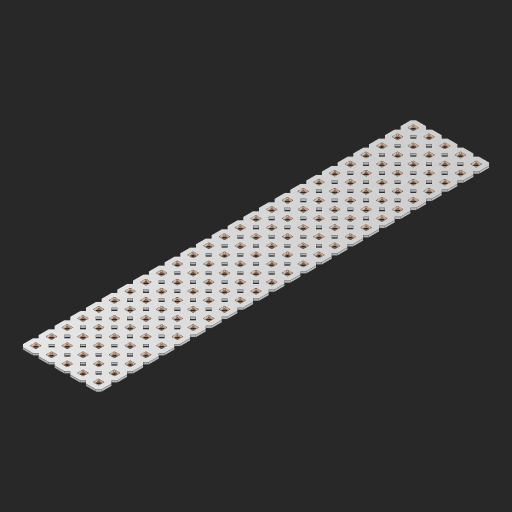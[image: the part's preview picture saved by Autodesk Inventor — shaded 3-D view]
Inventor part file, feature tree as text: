
AUTODESK INVENTOR PART (.ipt)
format: ipt  version: 2023 (Build 270158000, 158)  size: 1,711,616 bytes
history: native  units: in
note: dims shown in document units (in); Inventor stores cm internally (conversion verified against a paired STEP export)
features: other x357, extrude x124, sketch x2, pattern_linear x1
ambient origin geometry x8: Origin, YZ Plane, XZ Plane, XY Plane, X Axis, Y Axis, Z Axis, Center Point
bodies: Solid1 (feature_tree), Body (feature_tree)
feature tree (484):
  other  "Table"
  other  "Alu Plate 5x25"
  other  "Alu Plate 5x24"
  other  "Alu Plate 5x23"
  other  "Alu Plate 5x22"
  other  "Alu Plate 5x21"
  other  "Alu Plate 5x20"
  other  "Alu Plate 5x19"
  other  "Alu Plate 5x18"
  other  "Alu Plate 5x17"
  other  "Alu Plate 5x16"
  other  "Alu Plate 5x15"
  other  "Alu Plate 5x14"
  other  "Alu Plate 5x13"
  other  "Alu Plate 5x12"
  other  "Alu Plate 5x11"
  other  "Alu Plate 5x10"
  other  "Alu Plate 5x9"
  other  "Alu Plate 5x8"
  other  "Alu Plate 5x7"
  other  "Alu Plate 5x6"
  other  "Alu Plate 5x5"
  other  "Alu Plate 4x25"
  other  "Alu Plate 4x24"
  other  "Alu Plate 4x23"
  other  "Alu Plate 4x22"
  other  "Alu Plate 4x21"
  other  "Alu Plate 4x20"
  other  "Alu Plate 4x19"
  other  "Alu Plate 4x18"
  other  "Alu Plate 4x17"
  other  "Alu Plate 4x16"
  other  "Alu Plate 4x15"
  other  "Alu Plate 4x14"
  other  "Alu Plate 4x13"
  other  "Alu Plate 4x12"
  other  "Alu Plate 4x11"
  other  "Alu Plate 4x10"
  other  "Alu Plate 4x9"
  other  "Alu Plate 4x8"
  other  "Alu Plate 4x7"
  other  "Alu Plate 4x6"
  other  "Alu Plate 4x5"
  other  "Alu Plate 4x4"
  other  "Alu Plate 3x25"
  other  "Alu Plate 3x24"
  other  "Alu Plate 3x23"
  other  "Alu Plate 3x22"
  other  "Alu Plate 3x21"
  other  "Alu Plate 3x20"
  other  "Alu Plate 3x19"
  other  "Alu Plate 3x18"
  other  "Alu Plate 3x17"
  other  "Alu Plate 3x16"
  other  "Alu Plate 3x15"
  other  "Alu Plate 3x14"
  other  "Alu Plate 3x13"
  other  "Alu Plate 3x12"
  other  "Alu Plate 3x11"
  other  "Alu Plate 3x10"
  other  "Alu Plate 3x9"
  other  "Alu Plate 3x8"
  other  "Alu Plate 3x7"
  other  "Alu Plate 3x6"
  other  "Alu Plate 3x5"
  other  "Alu Plate 3x4"
  other  "Alu Plate 3x3"
  other  "Alu Plate 2x25"
  other  "Alu Plate 2x24"
  other  "Alu Plate 2x23"
  other  "Alu Plate 2x22"
  other  "Alu Plate 2x21"
  other  "Alu Plate 2x20"
  other  "Alu Plate 2x19"
  other  "Alu Plate 2x18"
  other  "Alu Plate 2x17"
  other  "Alu Plate 2x16"
  other  "Alu Plate 2x15"
  other  "Alu Plate 2x14"
  other  "Alu Plate 2x13"
  other  "Alu Plate 2x12"
  other  "Alu Plate 2x11"
  other  "Alu Plate 2x10"
  other  "Alu Plate 2x9"
  other  "Alu Plate 2x8"
  other  "Alu Plate 2x7"
  other  "Alu Plate 2x6"
  other  "Alu Plate 2x5"
  other  "Alu Plate 2x4"
  other  "Alu Plate 2x3"
  other  "Alu Plate 2x2"
  other  "Alu Plate 1x25"
  other  "Alu Plate 1x24"
  other  "Alu Plate 1x23"
  other  "Alu Plate 1x22"
  other  "Alu Plate 1x21"
  other  "Alu Plate 1x20"
  other  "Alu Plate 1x19"
  other  "Alu Plate 1x18"
  other  "Alu Plate 1x17"
  other  "Alu Plate 1x16"
  other  "Alu Plate 1x15"
  other  "Alu Plate 1x14"
  other  "Alu Plate 1x13"
  other  "Alu Plate 1x12"
  other  "Alu Plate 1x11"
  other  "Alu Plate 1x10"
  other  "Alu Plate 1x9"
  other  "Alu Plate 1x8"
  other  "Alu Plate 1x7"
  other  "Alu Plate 1x6"
  other  "Alu Plate 1x5"
  other  "Alu Plate 1x4"
  other  "Alu Plate 1x3"
  other  "Alu Plate 1x2"
  other  "Alu Plate 1x1"
  other  "Steel Plate 5x25"
  other  "Steel Plate 5x24"
  other  "Steel Plate 5x23"
  other  "Steel Plate 5x22"
  other  "Steel Plate 5x21"
  other  "Steel Plate 5x20"
  other  "Steel Plate 5x19"
  other  "Steel Plate 5x18"
  other  "Steel Plate 5x17"
  other  "Steel Plate 5x16"
  other  "Steel Plate 5x15"
  other  "Steel Plate 5x14"
  other  "Steel Plate 5x13"
  other  "Steel Plate 5x12"
  other  "Steel Plate 5x11"
  other  "Steel Plate 5x10"
  other  "Steel Plate 5x9"
  other  "Steel Plate 5x8"
  other  "Steel Plate 5x7"
  other  "Steel Plate 5x6"
  other  "Steel Plate 5x5"
  other  "Steel Plate 4x25"
  other  "Steel Plate 4x24"
  other  "Steel Plate 4x23"
  other  "Steel Plate 4x22"
  other  "Steel Plate 4x21"
  other  "Steel Plate 4x20"
  other  "Steel Plate 4x19"
  other  "Steel Plate 4x18"
  other  "Steel Plate 4x17"
  other  "Steel Plate 4x16"
  other  "Steel Plate 4x15"
  other  "Steel Plate 4x14"
  other  "Steel Plate 4x13"
  other  "Steel Plate 4x12"
  other  "Steel Plate 4x11"
  other  "Steel Plate 4x10"
  other  "Steel Plate 4x9"
  other  "Steel Plate 4x8"
  other  "Steel Plate 4x7"
  other  "Steel Plate 4x6"
  other  "Steel Plate 4x5"
  other  "Steel Plate 4x4"
  other  "Steel Plate 3x25"
  other  "Steel Plate 3x24"
  other  "Steel Plate 3x23"
  other  "Steel Plate 3x22"
  other  "Steel Plate 3x21"
  other  "Steel Plate 3x20"
  other  "Steel Plate 3x19"
  other  "Steel Plate 3x18"
  other  "Steel Plate 3x17"
  other  "Steel Plate 3x16"
  other  "Steel Plate 3x15"
  other  "Steel Plate 3x14"
  other  "Steel Plate 3x13"
  other  "Steel Plate 3x12"
  other  "Steel Plate 3x11"
  other  "Steel Plate 3x10"
  other  "Steel Plate 3x9"
  other  "Steel Plate 3x8"
  other  "Steel Plate 3x7"
  other  "Steel Plate 3x6"
  other  "Steel Plate 3x5"
  other  "Steel Plate 3x4"
  other  "Steel Plate 3x3"
  other  "Steel Plate 2x25"
  other  "Steel Plate 2x24"
  other  "Steel Plate 2x23"
  other  "Steel Plate 2x22"
  other  "Steel Plate 2x21"
  other  "Steel Plate 2x20"
  other  "Steel Plate 2x19"
  other  "Steel Plate 2x18"
  other  "Steel Plate 2x17"
  other  "Steel Plate 2x16"
  other  "Steel Plate 2x15"
  other  "Steel Plate 2x14"
  other  "Steel Plate 2x13"
  other  "Steel Plate 2x12"
  other  "Steel Plate 2x11"
  other  "Steel Plate 2x10"
  other  "Steel Plate 2x9"
  other  "Steel Plate 2x8"
  other  "Steel Plate 2x7"
  other  "Steel Plate 2x6"
  other  "Steel Plate 2x5"
  other  "Steel Plate 2x4"
  other  "Steel Plate 2x3"
  other  "Steel Plate 2x2"
  other  "Steel Plate 1x25"
  other  "Steel Plate 1x24"
  other  "Steel Plate 1x23"
  other  "Steel Plate 1x22"
  other  "Steel Plate 1x21"
  other  "Steel Plate 1x20"
  other  "Steel Plate 1x19"
  other  "Steel Plate 1x18"
  other  "Steel Plate 1x17"
  other  "Steel Plate 1x16"
  other  "Steel Plate 1x15"
  other  "Steel Plate 1x14"
  other  "Steel Plate 1x13"
  other  "Steel Plate 1x12"
  other  "Steel Plate 1x11"
  other  "Steel Plate 1x10"
  other  "Steel Plate 1x9"
  other  "Steel Plate 1x8"
  other  "Steel Plate 1x7"
  other  "Steel Plate 1x6"
  other  "Steel Plate 1x5"
  other  "Steel Plate 1x4"
  other  "Steel Plate 1x3"
  other  "Steel Plate 1x2"
  other  "Steel Plate 1x1"
  pattern_linear  "Rectangular Pattern1"  Spacing1=0.09in  [1 undecoded]
  sketch  "Sketch1"  dims[d1=0.5in]
  sketch  "Sketch2"  dims[d2=0.182in d3=0.09in d4=0.09in d5=0.09in d6=0.09in d7=0.09in d8=0.09in d9=0.09in d10=0.09in d11=0.02in d13=0.0in d14=0.172in d15=0.0625in d16=0.0in d19=0.5in d22=0.5in]
  other  "Srf1"
  other  "Srf126"
  other  "Srf127"
  other  "Srf128"
  other  "Srf129"
  other  "Srf130"
  other  "Srf131"
  other  "Srf250"
  other  "Srf251"
  other  "Srf252"
  other  "Srf253"
  other  "Srf254"
  other  "Srf255"
  other  "Srf256"
  other  "Srf257"
  other  "Srf258"
  other  "Srf259"
  other  "Srf260"
  other  "Srf261"
  other  "Srf262"
  other  "Srf263"
  other  "Srf264"
  other  "Srf265"
  other  "Srf266"
  other  "Srf267"
  other  "Srf268"
  other  "Srf269"
  other  "Srf270"
  other  "Srf271"
  other  "Srf272"
  other  "Srf273"
  other  "Srf274"
  other  "Srf275"
  other  "Srf276"
  other  "Srf277"
  other  "Srf278"
  other  "Srf279"
  other  "Srf280"
  other  "Srf281"
  other  "Srf282"
  other  "Srf283"
  other  "Srf284"
  other  "Srf285"
  other  "Srf286"
  other  "Srf287"
  other  "Srf288"
  other  "Srf289"
  other  "Srf290"
  other  "Srf291"
  other  "Srf292"
  other  "Srf293"
  other  "Srf294"
  other  "Srf295"
  other  "Srf296"
  other  "Srf297"
  other  "Srf298"
  other  "Srf299"
  other  "Srf300"
  other  "Srf301"
  other  "Srf302"
  other  "Srf303"
  other  "Srf304"
  other  "Srf305"
  other  "Srf306"
  other  "Srf307"
  other  "Srf308"
  other  "Srf309"
  other  "Srf310"
  other  "Srf311"
  other  "Srf312"
  other  "Srf313"
  other  "Srf314"
  other  "Srf315"
  other  "Srf316"
  other  "Srf317"
  other  "Srf318"
  other  "Srf319"
  other  "Srf320"
  other  "Srf321"
  other  "Srf322"
  other  "Srf323"
  other  "Srf324"
  other  "Srf325"
  other  "Srf326"
  other  "Srf327"
  other  "Srf328"
  other  "Srf329"
  other  "Srf330"
  other  "Srf331"
  other  "Srf332"
  other  "Srf333"
  other  "Srf334"
  other  "Srf335"
  other  "Srf336"
  other  "Srf337"
  other  "Srf338"
  other  "Srf339"
  other  "Srf340"
  other  "Srf341"
  other  "Srf342"
  other  "Srf343"
  other  "Srf344"
  other  "Srf345"
  other  "Srf346"
  other  "Srf347"
  other  "Srf348"
  other  "Srf349"
  other  "Srf350"
  other  "Srf351"
  other  "Srf352"
  other  "Srf353"
  other  "Srf354"
  other  "Srf355"
  other  "Srf356"
  other  "Srf357"
  other  "Srf358"
  other  "Srf359"
  other  "Srf360"
  other  "Srf361"
  other  "Srf362"
  other  "Srf363"
  other  "Srf364"
  other  "Srf365"
  other  "Srf366"
  other  "Srf367"
  other  "Circle"
  extrude  "ExtrusionSrf126"  Depth=0.09in
  extrude  "ExtrusionSrf127"  Depth=0.09in
  extrude  "ExtrusionSrf128"  Depth=0.09in
  extrude  "ExtrusionSrf129"  Depth=0.09in
  extrude  "ExtrusionSrf130"  Depth=0.09in
  extrude  "ExtrusionSrf131"  Depth=0.09in
  extrude  "ExtrusionSrf250"  Depth=0.09in
  extrude  "ExtrusionSrf251"  Depth=0.02in
  extrude  "ExtrusionSrf252"  TaperAngle=0.0deg  [1 undecoded]
  extrude  "ExtrusionSrf253"  Depth=0.5in
  extrude  "ExtrusionSrf254"  Depth=0.0625in TaperAngle=0.0deg
  extrude  "ExtrusionSrf255"  Depth=0.5in
  extrude  "ExtrusionSrf256"  Depth=0.5in
  extrude  "ExtrusionSrf257"  [1 undecoded]
  extrude  "ExtrusionSrf258"  [1 undecoded]
  extrude  "ExtrusionSrf259"  [1 undecoded]
  extrude  "ExtrusionSrf260"  [1 undecoded]
  extrude  "ExtrusionSrf261"  [1 undecoded]
  extrude  "ExtrusionSrf262"  [1 undecoded]
  extrude  "ExtrusionSrf263"  [1 undecoded]
  extrude  "ExtrusionSrf264"  [1 undecoded]
  extrude  "ExtrusionSrf265"  [1 undecoded]
  extrude  "ExtrusionSrf266"  [1 undecoded]
  extrude  "ExtrusionSrf267"  [1 undecoded]
  extrude  "ExtrusionSrf268"  [1 undecoded]
  extrude  "ExtrusionSrf269"  [1 undecoded]
  extrude  "ExtrusionSrf270"  [1 undecoded]
  extrude  "ExtrusionSrf271"  [1 undecoded]
  extrude  "ExtrusionSrf272"  [1 undecoded]
  extrude  "ExtrusionSrf273"  [1 undecoded]
  extrude  "ExtrusionSrf274"  [1 undecoded]
  extrude  "ExtrusionSrf275"  [1 undecoded]
  extrude  "ExtrusionSrf276"  [1 undecoded]
  extrude  "ExtrusionSrf277"  [1 undecoded]
  extrude  "ExtrusionSrf278"  [1 undecoded]
  extrude  "ExtrusionSrf279"  [1 undecoded]
  extrude  "ExtrusionSrf280"  [1 undecoded]
  extrude  "ExtrusionSrf281"  [1 undecoded]
  extrude  "ExtrusionSrf282"  [1 undecoded]
  extrude  "ExtrusionSrf283"  [1 undecoded]
  extrude  "ExtrusionSrf284"  [1 undecoded]
  extrude  "ExtrusionSrf285"  [1 undecoded]
  extrude  "ExtrusionSrf286"  [1 undecoded]
  extrude  "ExtrusionSrf287"  [1 undecoded]
  extrude  "ExtrusionSrf288"  [1 undecoded]
  extrude  "ExtrusionSrf289"  [1 undecoded]
  extrude  "ExtrusionSrf290"  [1 undecoded]
  extrude  "ExtrusionSrf291"  [1 undecoded]
  extrude  "ExtrusionSrf292"  [1 undecoded]
  extrude  "ExtrusionSrf293"  [1 undecoded]
  extrude  "ExtrusionSrf294"  [1 undecoded]
  extrude  "ExtrusionSrf295"  [1 undecoded]
  extrude  "ExtrusionSrf296"  [1 undecoded]
  extrude  "ExtrusionSrf297"  [1 undecoded]
  extrude  "ExtrusionSrf298"  [1 undecoded]
  extrude  "ExtrusionSrf299"  [1 undecoded]
  extrude  "ExtrusionSrf300"  [1 undecoded]
  extrude  "ExtrusionSrf301"  [1 undecoded]
  extrude  "ExtrusionSrf302"  [1 undecoded]
  extrude  "ExtrusionSrf303"  [1 undecoded]
  extrude  "ExtrusionSrf304"  [1 undecoded]
  extrude  "ExtrusionSrf305"  [1 undecoded]
  extrude  "ExtrusionSrf306"  [1 undecoded]
  extrude  "ExtrusionSrf307"  [1 undecoded]
  extrude  "ExtrusionSrf308"  [1 undecoded]
  extrude  "ExtrusionSrf309"  [1 undecoded]
  extrude  "ExtrusionSrf310"  [1 undecoded]
  extrude  "ExtrusionSrf311"  [1 undecoded]
  extrude  "ExtrusionSrf312"  [1 undecoded]
  extrude  "ExtrusionSrf313"  [1 undecoded]
  extrude  "ExtrusionSrf314"  [1 undecoded]
  extrude  "ExtrusionSrf315"  [1 undecoded]
  extrude  "ExtrusionSrf316"  [1 undecoded]
  extrude  "ExtrusionSrf317"  [1 undecoded]
  extrude  "ExtrusionSrf318"  [1 undecoded]
  extrude  "ExtrusionSrf319"  [1 undecoded]
  extrude  "ExtrusionSrf320"  [1 undecoded]
  extrude  "ExtrusionSrf321"  [1 undecoded]
  extrude  "ExtrusionSrf322"  [1 undecoded]
  extrude  "ExtrusionSrf323"  [1 undecoded]
  extrude  "ExtrusionSrf324"  [1 undecoded]
  extrude  "ExtrusionSrf325"  [1 undecoded]
  extrude  "ExtrusionSrf326"  [1 undecoded]
  extrude  "ExtrusionSrf327"  [1 undecoded]
  extrude  "ExtrusionSrf328"  [1 undecoded]
  extrude  "ExtrusionSrf329"  [1 undecoded]
  extrude  "ExtrusionSrf330"  [1 undecoded]
  extrude  "ExtrusionSrf331"  [1 undecoded]
  extrude  "ExtrusionSrf332"  [1 undecoded]
  extrude  "ExtrusionSrf333"  [1 undecoded]
  extrude  "ExtrusionSrf334"  [1 undecoded]
  extrude  "ExtrusionSrf335"  [1 undecoded]
  extrude  "ExtrusionSrf336"  [1 undecoded]
  extrude  "ExtrusionSrf337"  [1 undecoded]
  extrude  "ExtrusionSrf338"  [1 undecoded]
  extrude  "ExtrusionSrf339"  [1 undecoded]
  extrude  "ExtrusionSrf340"  [1 undecoded]
  extrude  "ExtrusionSrf341"  [1 undecoded]
  extrude  "ExtrusionSrf342"  [1 undecoded]
  extrude  "ExtrusionSrf343"  [1 undecoded]
  extrude  "ExtrusionSrf344"  [1 undecoded]
  extrude  "ExtrusionSrf345"  [1 undecoded]
  extrude  "ExtrusionSrf346"  [1 undecoded]
  extrude  "ExtrusionSrf347"  [1 undecoded]
  extrude  "ExtrusionSrf348"  [1 undecoded]
  extrude  "ExtrusionSrf349"  [1 undecoded]
  extrude  "ExtrusionSrf350"  [1 undecoded]
  extrude  "ExtrusionSrf351"  [1 undecoded]
  extrude  "ExtrusionSrf352"  [1 undecoded]
  extrude  "ExtrusionSrf353"  [1 undecoded]
  extrude  "ExtrusionSrf354"  [1 undecoded]
  extrude  "ExtrusionSrf355"  [1 undecoded]
  extrude  "ExtrusionSrf356"  [1 undecoded]
  extrude  "ExtrusionSrf357"  [1 undecoded]
  extrude  "ExtrusionSrf358"  [1 undecoded]
  extrude  "ExtrusionSrf359"  [1 undecoded]
  extrude  "ExtrusionSrf360"  [1 undecoded]
  extrude  "ExtrusionSrf361"  [1 undecoded]
  extrude  "ExtrusionSrf362"  [1 undecoded]
  extrude  "ExtrusionSrf363"  [1 undecoded]
  extrude  "ExtrusionSrf364"  [1 undecoded]
  extrude  "ExtrusionSrf365"  [1 undecoded]
  extrude  "ExtrusionSrf366"  [1 undecoded]
  extrude  "ExtrusionSrf367"  [1 undecoded]
note: 113 required parameter values undecoded (feature->parameter linkage not recoverable at this tier; creation-order binding heuristic only, values carry confidence <= 0.55)
